# Revit family: Towel_Bar-American_Standard-Aspirations-70610XX_Series
name_source: partatom
category: Specialty Equipment
units: mm (PartAtom-declared; Revit-internal decimal feet)

## family parameters
Cut with Voids When Loaded = No
Host = Face
OmniClass Number = 23.40.20.21.27
OmniClass Title = Towel Bars
Part Type = Normal
Room Calculation Point = No
Round Connector Dimension = Use Diameter
Shared = Yes

## types (6) — shared parameters
Assembly Code = C1030220
Default Elevation = 40"
Installation Type = Wall Mounted
Manufacturer = American Standard
URL = http://www.americanstandard-us.com

## per-type parameters (varying)
| type | Description | Finish | Length | Length/2 | Material |
| 7061018.002 | Aspirations 18-inch Towel Bar | Metal-American Standard-002-Polished Chrome | 18" | 9" | Metal-American Standard-002-Polished Chrome |
| 7061018.295 | Aspirations 18-inch Towel Bar | Metal-American Standard-295-Brushed Nickel | 18" | 9" | Metal-American Standard-295-Brushed Nickel |
| 7061018.243 | Aspirations 18-inch Towel Bar | Metal-American Standard-243-Matte Black | 18" | 9" | Metal-American Standard-243-Matte Black |
| 7061024.002 | Aspirations 24-inch Towel Bar | Metal-American Standard-002-Polished Chrome | 24" | 12" | Metal-American Standard-002-Polished Chrome |
| 7061024.243 | Aspirations 24-inch Towel Bar | Metal-American Standard-243-Matte Black | 24" | 12" | Metal-American Standard-243-Matte Black |
| 7061024.295 | Aspirations 24-inch Towel Bar | Metal-American Standard-295-Brushed Nickel | 24" | 12" | Metal-American Standard-295-Brushed Nickel |

note: column(s) folded — value = type name in every type: Model

## geometry (parser evidence)
native form markers: Sweep x3
no freeform markers — native parametric forms only
